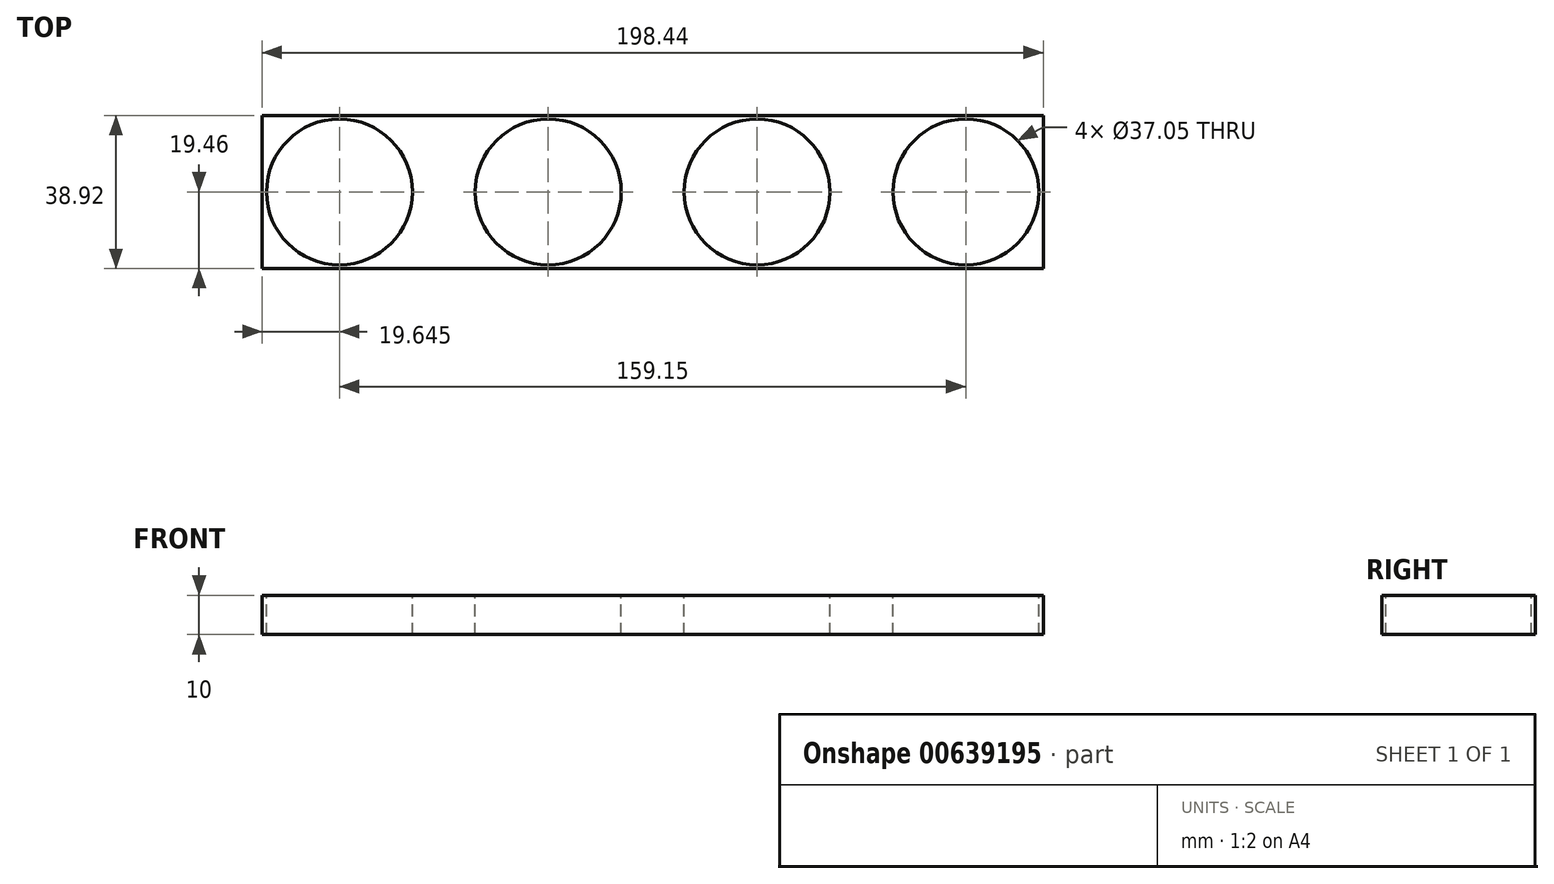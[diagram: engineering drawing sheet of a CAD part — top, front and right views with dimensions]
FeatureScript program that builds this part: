
annotation { "Feature Type Name" : "Feature", "Feature Type Description" : "" }
export const myFeature = defineFeature(function(context is Context, id is Id, definition is map)
    precondition{}
    {
        {
            var Q0;
            Q0=qCreatedBy(makeId("Top.planeOp"),FACE);
            var sketch = newSketch(context, id + "F0", { "sketchPlane" : qUnion([Q0])});
            skCircle(sketch, "E0", {"center": v(-79.58, 0) * mm, "radius": 18.52 * mm});
            skCircle(sketch, "E1", {"center": v(-26.52, 0) * mm, "radius": 18.52 * mm});
            skCircle(sketch, "E2.MirrorC", {"center": v(26.52, 0) * mm, "radius": 18.52 * mm});
            skCircle(sketch, "E3.MirrorC", {"center": v(79.58, 0) * mm, "radius": 18.52 * mm});
            skCircle(sketch, "E4", {"center": v(-79.58, 0) * mm, "radius": 10.53 * mm});
            skCircle(sketch, "E5", {"center": v(-26.52, 0) * mm, "radius": 10.53 * mm});
            skCircle(sketch, "E6", {"center": v(26.52, 0) * mm, "radius": 10.53 * mm});
            skCircle(sketch, "E7", {"center": v(79.58, 0) * mm, "radius": 10.53 * mm});
            skLineSegment(sketch, "E8.bottom", {"start": v(99.22, -19.46) * mm, "end": v(-99.22, -19.46) * mm});
            skLineSegment(sketch, "E8.top", {"start": v(99.22, 19.46) * mm, "end": v(-99.22, 19.46) * mm});
            skLineSegment(sketch, "E8.left", {"start": v(99.22, -19.46) * mm, "end": v(99.22, 19.46) * mm});
            skLineSegment(sketch, "E8.right", {"start": v(-99.22, -19.46) * mm, "end": v(-99.22, 19.46) * mm});
            skPoint(sketch, "E8.middle", {"position": v(0, 0) * mm});
            skSolve(sketch);
        }
        {
            var Q0;
            Q0=makeQuery(id+"F0.imprint","IMPRINT",FACE,{"disambiguationData":[TD([[makeQuery(id+"F0.imprint","IMPRINT",EDGE,{"derivedFrom":sQuery(id+"F0.wireOp",EDGE,"E0")}),-1.0]])]});
            extrude(context, id + "F1", {"entities" : qUnion([Q0]), "oppositeDirection" : true, "depth" : 10 * mm, "offsetDistance" : 25 * mm});
        }
    });
